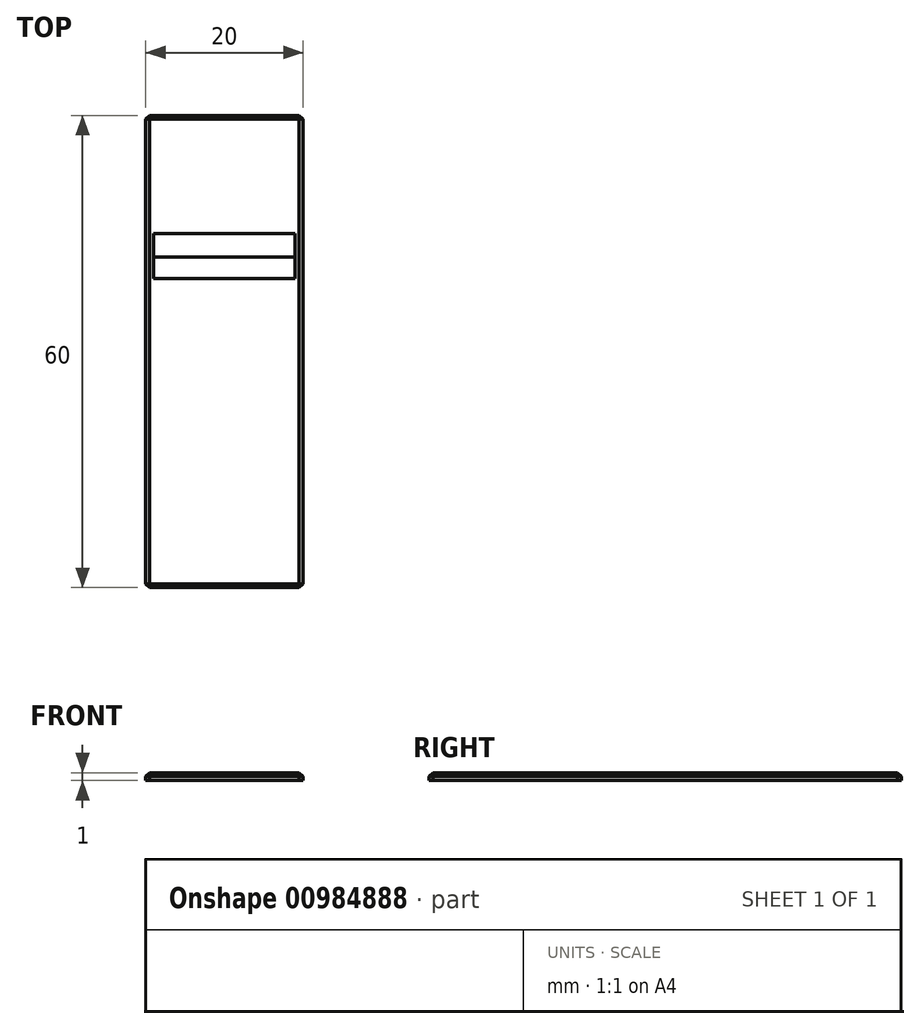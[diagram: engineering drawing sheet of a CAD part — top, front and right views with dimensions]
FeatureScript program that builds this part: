
annotation { "Feature Type Name" : "Feature", "Feature Type Description" : "" }
export const myFeature = defineFeature(function(context is Context, id is Id, definition is map)
    precondition{}
    {
        {
            var Q0;
            Q0=qCreatedBy(makeId("Top.planeOp"),FACE);
            var sketch = newSketch(context, id + "F0", { "sketchPlane" : qUnion([Q0])});
            skLineSegment(sketch, "E0.bottom", {"start": v(10, -30) * mm, "end": v(-10, -30) * mm});
            skLineSegment(sketch, "E0.top", {"start": v(10, 30) * mm, "end": v(-10, 30) * mm});
            skLineSegment(sketch, "E0.left", {"start": v(10, -30) * mm, "end": v(10, 30) * mm});
            skLineSegment(sketch, "E0.right", {"start": v(-10, -30) * mm, "end": v(-10, 30) * mm});
            skPoint(sketch, "E0.middle", {"position": v(0, 0) * mm});
            skSolve(sketch);
        }
        {
            var Q0;
            Q0 = qSketchRegion(id + "F0", true);
            extrude(context, id + "F1", {"entities" : qUnion([Q0]), "depth" : 1 * mm, "offsetDistance" : 25 * mm});
        }
        {
            var Q0;
            Q0=qCreatedBy(makeId("Right.planeOp"),FACE);
            var sketch = newSketch(context, id + "F2", { "sketchPlane" : qUnion([Q0])});
            skLineSegment(sketch, "E1", {"start": v(12, 0) * mm, "end": v(15, 0) * mm});
            skLineSegment(sketch, "E2", {"start": v(15, 0) * mm, "end": v(15, 1) * mm});
            skLineSegment(sketch, "E3", {"start": v(15, 1) * mm, "end": v(9.25, 1) * mm});
            skLineSegment(sketch, "E4", {"start": v(9.25, 1) * mm, "end": v(12, 0) * mm});
            skSolve(sketch);
        }
        {
            var Q0;
            Q0=makeQuery(id+"F2.imprint","IMPRINT",FACE,{"disambiguationData":[TD([[makeQuery(id+"F2.imprint","IMPRINT",EDGE,{"derivedFrom":sQuery(id+"F2.wireOp",EDGE,"E1")}),1.0]])]});
            extrude(context, id + "F3", {"entities" : qUnion([Q0]), "operationType" : NewBodyOperationType.REMOVE, "endBound" : BoundingType.SYMMETRIC, "oppositeDirection" : true, "depth" : 18 * mm, "offsetDistance" : 25 * mm});
        }
        {
            var Q0;
            Q0=makeQuery(id+"F1.opExtrude","CAP_EDGE",EDGE,{"disambiguationData":[OSD([sQuery(id+"F0.wireOp",EDGE,"E0.left")])],"isStart":false});
            var Q1;
            Q1=makeQuery(id+"F1.opExtrude","CAP_EDGE",EDGE,{"disambiguationData":[OSD([sQuery(id+"F0.wireOp",EDGE,"E0.bottom")])],"isStart":false});
            var Q2;
            Q2=makeQuery(id+"F1.opExtrude","CAP_EDGE",EDGE,{"disambiguationData":[OSD([sQuery(id+"F0.wireOp",EDGE,"E0.right")])],"isStart":false});
            var Q3;
            Q3=makeQuery(id+"F1.opExtrude","CAP_EDGE",EDGE,{"disambiguationData":[OSD([sQuery(id+"F0.wireOp",EDGE,"E0.top")])],"isStart":false});
            var Q4;
            Q4=makeQuery(id+"F1.opExtrude","SWEPT_EDGE",EDGE,{"disambiguationData":[OSD([sQuery(id+"F0.wireOp",EDGE,"E0.bottom"),sQuery(id+"F0.wireOp",EDGE,"E0.left")])]});
            var Q5;
            Q5=makeQuery(id+"F1.opExtrude","SWEPT_EDGE",EDGE,{"disambiguationData":[OSD([sQuery(id+"F0.wireOp",EDGE,"E0.top"),sQuery(id+"F0.wireOp",EDGE,"E0.left")])]});
            var Q6;
            Q6=makeQuery(id+"F1.opExtrude","SWEPT_EDGE",EDGE,{"disambiguationData":[OSD([sQuery(id+"F0.wireOp",EDGE,"E0.top"),sQuery(id+"F0.wireOp",EDGE,"E0.right")])]});
            var Q7;
            Q7=makeQuery(id+"F1.opExtrude","SWEPT_EDGE",EDGE,{"disambiguationData":[OSD([sQuery(id+"F0.wireOp",EDGE,"E0.bottom"),sQuery(id+"F0.wireOp",EDGE,"E0.right")])]});
            chamfer(context, id + "F4", {"entities" : qUnion([Q0, Q1, Q2, Q3, Q4, Q5, Q6, Q7]), "width" : 0.5 * mm, "tangentPropagation" : true});
        }
    });
